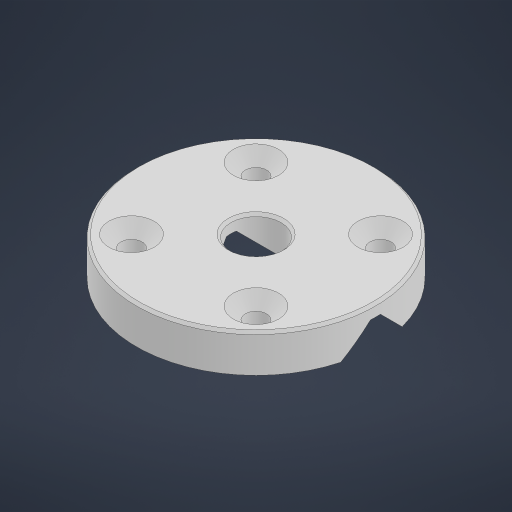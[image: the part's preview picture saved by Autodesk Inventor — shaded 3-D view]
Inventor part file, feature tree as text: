
AUTODESK INVENTOR PART (.ipt)
format: ipt  version: 2024.3 (Build 283343000, 343)  size: 242,688 bytes
history: native  units: mm
features: sketch x4, extrude x2, chamfer x2, hole x1, projected_geometry x1
ambient origin geometry x8: Origin, YZ Plane, XZ Plane, XY Plane, X Axis, Y Axis, Z Axis, Center Point
bodies: Solid1 (feature_tree)
feature tree (10):
  sketch  "Sketch1"  dims[d0=95.0mm d1=20.0mm]
  extrude  "Extrusion1"  Depth=20.0mm
  hole  "Hole1"  [1 undecoded]
  extrude  "Extrusion2"  Depth=30.0mm
  chamfer  "Chamfer1"  Angle=45.0deg  [1 undecoded]
  chamfer  "Chamfer3"  Distance=4.0mm
  sketch  "Sketch3"  dims[d5=8.5mm d6=18.0mm d7=18.0mm d8=2.0mm d9=90.0deg d10=20.4mm d11=20.594885mm d12=30.0mm]
  sketch  "Sketch4"  dims[d13=6.0mm d14=45.0deg d15=4.0mm d16=0.0mm d17=0.0mm d18=1.0mm d19=2.0mm d20=45.0deg d24=0.5mm d25=2.0mm d26=45.0deg d27=5.0mm d29=5.0mm d30=5.0mm d31=4.443651mm d32=5.0mm]
  sketch  "Sketch2"  dims[d2=12.5mm d3=15.0mm d4=0.0mm]
  projected_geometry  "Projected Loop1"
note: 2 required parameter values undecoded (feature->parameter linkage not recoverable at this tier; creation-order binding heuristic only, values carry confidence <= 0.55)
